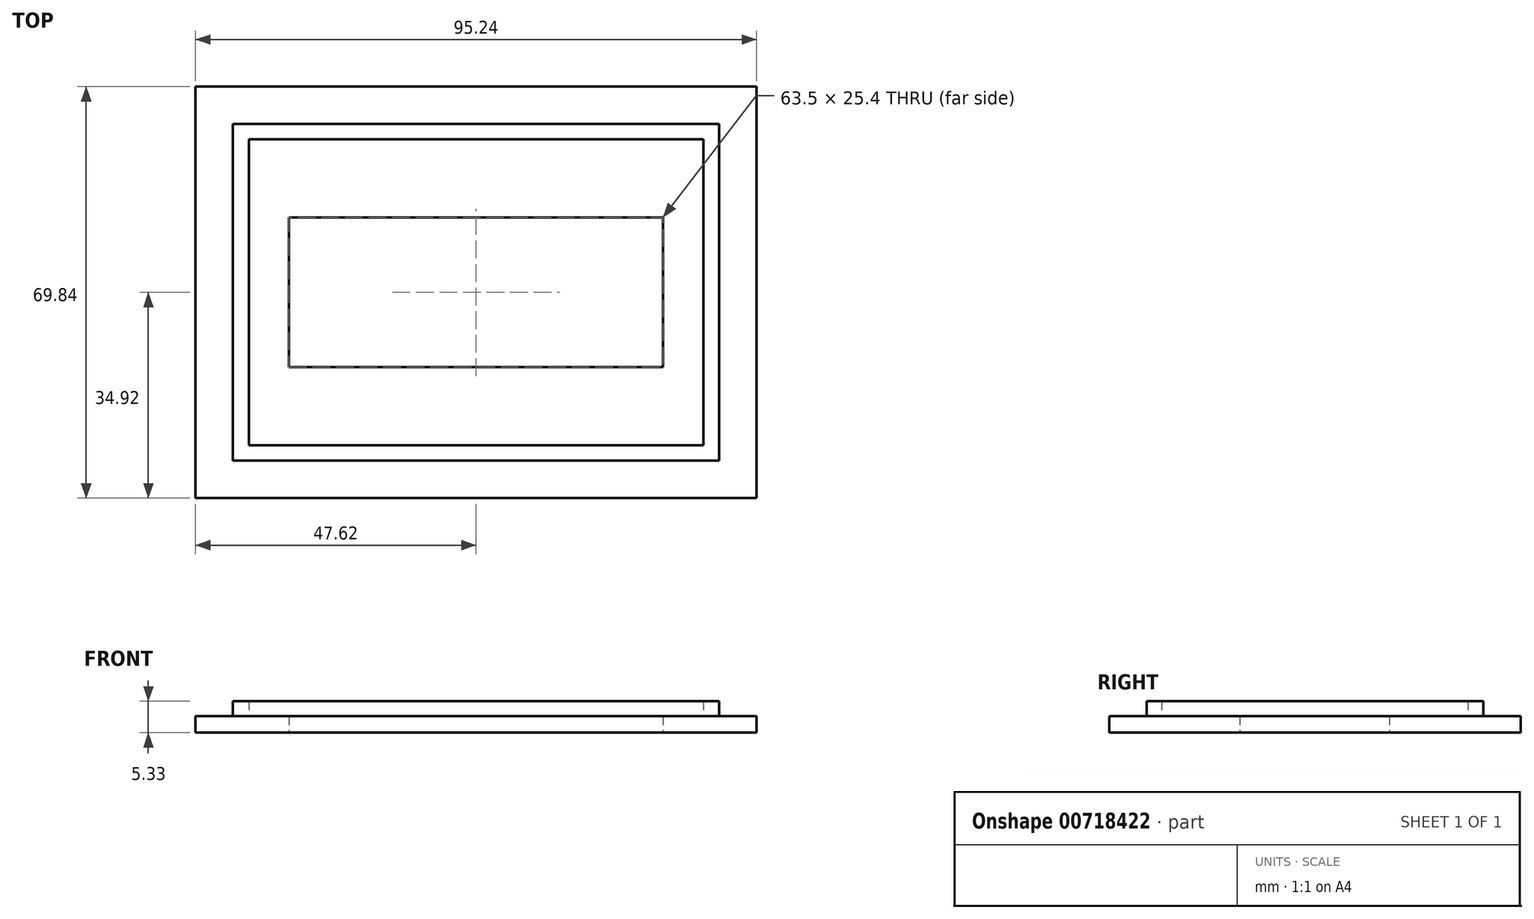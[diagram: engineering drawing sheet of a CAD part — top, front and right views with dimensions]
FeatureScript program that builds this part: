
annotation { "Feature Type Name" : "Feature", "Feature Type Description" : "" }
export const myFeature = defineFeature(function(context is Context, id is Id, definition is map)
    precondition{}
    {
        {
            var Q0;
            Q0=qCreatedBy(makeId("Top.planeOp"),FACE);
            var sketch = newSketch(context, id + "F0", { "sketchPlane" : qUnion([Q0])});
            skLineSegment(sketch, "E0.bottom", {"start": v(47.62, 34.93) * mm, "end": v(-47.63, 34.92) * mm});
            skLineSegment(sketch, "E0.top", {"start": v(47.63, -34.92) * mm, "end": v(-47.62, -34.93) * mm});
            skLineSegment(sketch, "E0.left", {"start": v(47.62, 34.93) * mm, "end": v(47.63, -34.92) * mm});
            skLineSegment(sketch, "E0.right", {"start": v(-47.63, 34.92) * mm, "end": v(-47.62, -34.93) * mm});
            skPoint(sketch, "E0.middle", {"position": v(0, 0) * mm});
            skLineSegment(sketch, "E1.bottom", {"start": v(41.27, 28.58) * mm, "end": v(-41.28, 28.57) * mm});
            skLineSegment(sketch, "E1.top", {"start": v(41.28, -28.57) * mm, "end": v(-41.28, -28.58) * mm});
            skLineSegment(sketch, "E1.left", {"start": v(41.27, 28.58) * mm, "end": v(41.28, -28.57) * mm});
            skLineSegment(sketch, "E1.right", {"start": v(-41.28, 28.57) * mm, "end": v(-41.28, -28.58) * mm});
            skLineSegment(sketch, "E2.bottom", {"start": v(31.75, 12.7) * mm, "end": v(-31.75, 12.7) * mm});
            skLineSegment(sketch, "E2.top", {"start": v(31.75, -12.7) * mm, "end": v(-31.75, -12.7) * mm});
            skLineSegment(sketch, "E2.left", {"start": v(31.75, 12.7) * mm, "end": v(31.75, -12.7) * mm});
            skLineSegment(sketch, "E2.right", {"start": v(-31.75, 12.7) * mm, "end": v(-31.75, -12.7) * mm});
            skLineSegment(sketch, "E3.bottom", {"start": v(38.59, 25.97) * mm, "end": v(-38.59, 25.97) * mm});
            skLineSegment(sketch, "E3.top", {"start": v(38.59, -25.97) * mm, "end": v(-38.59, -25.97) * mm});
            skLineSegment(sketch, "E3.left", {"start": v(38.59, 25.97) * mm, "end": v(38.59, -25.97) * mm});
            skLineSegment(sketch, "E3.right", {"start": v(-38.59, 25.97) * mm, "end": v(-38.59, -25.97) * mm});
            skSolve(sketch);
        }
        {
            var Q0;
            Q0 = qSketchRegion(id + "F0", true);
            extrude(context, id + "F1", {"entities" : qUnion([Q0]), "depth" : 2.8 * mm, "offsetDistance" : 25.4 * mm});
        }
        {
            var Q0;
            Q0=makeQuery(id+"F0.imprint","IMPRINT",FACE,{"disambiguationData":[TD([[makeQuery(id+"F0.imprint","IMPRINT",EDGE,{"derivedFrom":sQuery(id+"F0.wireOp",EDGE,"E1.bottom")}),1.0]])]});
            extrude(context, id + "F2", {"entities" : qUnion([Q0]), "operationType" : NewBodyOperationType.ADD, "depth" : 5.33 * mm, "offsetDistance" : 25.4 * mm});
        }
        {
            var Q0;
            Q0=makeQuery(id+"F0.imprint","IMPRINT",FACE,{"disambiguationData":[TD([[makeQuery(id+"F0.imprint","IMPRINT",EDGE,{"derivedFrom":sQuery(id+"F0.wireOp",EDGE,"E2.bottom")}),-1.0]])]});
            extrude(context, id + "F3", {"entities" : qUnion([Q0]), "operationType" : NewBodyOperationType.ADD, "depth" : 2.8 * mm, "offsetDistance" : 25.4 * mm});
        }
    });
